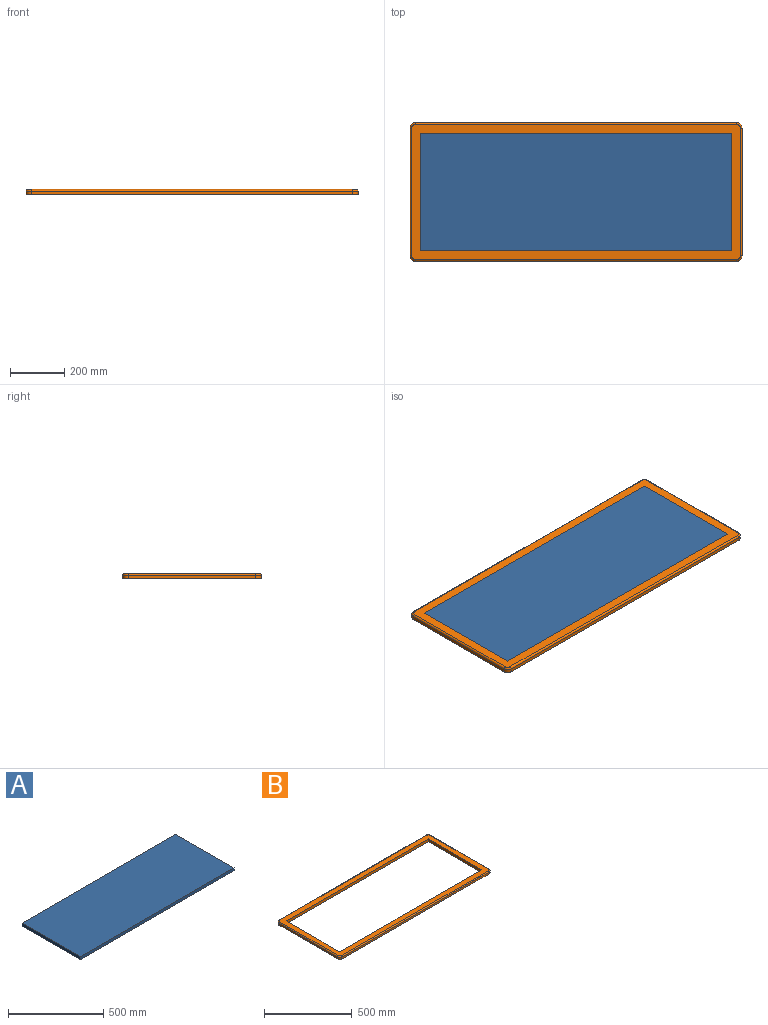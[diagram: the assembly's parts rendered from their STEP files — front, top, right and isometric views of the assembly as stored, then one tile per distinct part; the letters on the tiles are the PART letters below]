
ASSEMBLY  parts=2 mates=1
PART A: 6 faces, bbox 1143x431.8x19.1 mm
  f0: plane 1143x19.05mm, normal (0,1,0), area 21774.1mm2, adj f1,f3,f4,f5
  f1: plane 431.8x19.05mm, normal (-1,0,0), area 8225.8mm2, adj f0,f2,f4,f5
  f2: plane 1143x19.05mm, normal (0,-1,0), area 21774.1mm2, adj f1,f3,f4,f5
  f3: plane 431.8x19.05mm, normal (1,0,0), area 8225.8mm2, adj f0,f2,f4,f5
  f4: plane 1143x431.8mm, normal (0,0,1), area 493547.4mm2, adj f0,f1,f2,f3
  f5: plane 1143x431.8mm, normal (0,0,-1), area 493547.4mm2, adj f0,f1,f2,f3
PART B: 22 faces, bbox 1222.3x511.1x19.1 mm
  f0: plane 1181.1x12.7mm, normal (0,1,0), area 15000mm2, adj f9,f10,f13,f19
  f1: plane 469.9x12.7mm, normal (-1,0,0), area 5967.7mm2, adj f9,f10,f11,f20
  f2: plane 1181.1x12.7mm, normal (0,-1,0), area 15000mm2, adj f9,f11,f12,f16
  f3: plane 431.8x19.05mm, normal (1,0,0), area 8225.8mm2, adj f4,f6,f8,f9
  f4: plane 1143x19.05mm, normal (0,-1,0), area 21774.1mm2, adj f3,f5,f8,f9
  f5: plane 431.8x19.05mm, normal (-1,0,0), area 8225.8mm2, adj f4,f6,f8,f9
  f6: plane 1143x19.05mm, normal (0,1,0), area 21774.1mm2, adj f3,f5,f8,f9
  f7: plane 469.9x12.7mm, normal (1,0,0), area 5967.7mm2, adj f9,f12,f13,f15
  f8: plane 1206.5x495.3mm, normal (0,0,1), area 103893.6mm2, adj f3,f4,f5,f6,f14,f15,f16,f17
  f9: plane 1219.2x508mm, normal (0,0,-1), area 125494.7mm2, adj f0,f1,f2,f3,f4,f5,f6,f7
  f10: cylinder r=19.05mm len=19.05mm, axis (0,0,1), area 380mm2, adj f0,f1,f9,f21
  f11: cylinder r=19.05mm len=19.05mm, axis (0,0,-1), area 380mm2, adj f1,f2,f9,f18
  f12: cylinder r=19.05mm len=19.05mm, axis (0,0,1), area 380mm2, adj f2,f7,f9,f14
  f13: cylinder r=19.05mm len=19.05mm, axis (0,0,-1), area 380mm2, adj f0,f7,f9,f17
  f14: torus R=12.7mm, axis (0,0,1), area 262.3mm2, adj f8,f12,f15,f16
  f15: cylinder r=6.35mm len=469.9mm, axis (0,-1,0), area 4687mm2, adj f7,f8,f14,f17
  f16: cylinder r=6.35mm len=1181.1mm, axis (-1,0,0), area 11780.9mm2, adj f2,f8,f14,f18
  f17: torus R=12.7mm, axis (0,0,1), area 262.3mm2, adj f8,f13,f15,f19
  f18: torus R=12.7mm, axis (0,0,1), area 262.3mm2, adj f8,f11,f16,f20
  f19: cylinder r=6.35mm len=1181.1mm, axis (1,0,0), area 11780.9mm2, adj f0,f8,f17,f21
  f20: cylinder r=6.35mm len=469.9mm, axis (0,1,0), area 4687mm2, adj f1,f8,f18,f21
  f21: torus R=12.7mm, axis (0,0,1), area 262.3mm2, adj f8,f10,f19,f20
PLACE A t=(-193.06,-98.63,0.23)mm
PLACE B t=(-193.06,-98.63,0.23)mm
MATE parallel A.f4 <-> B.f8  axis (0,0,1) through (-193.06,-98.63,19.28)mm
